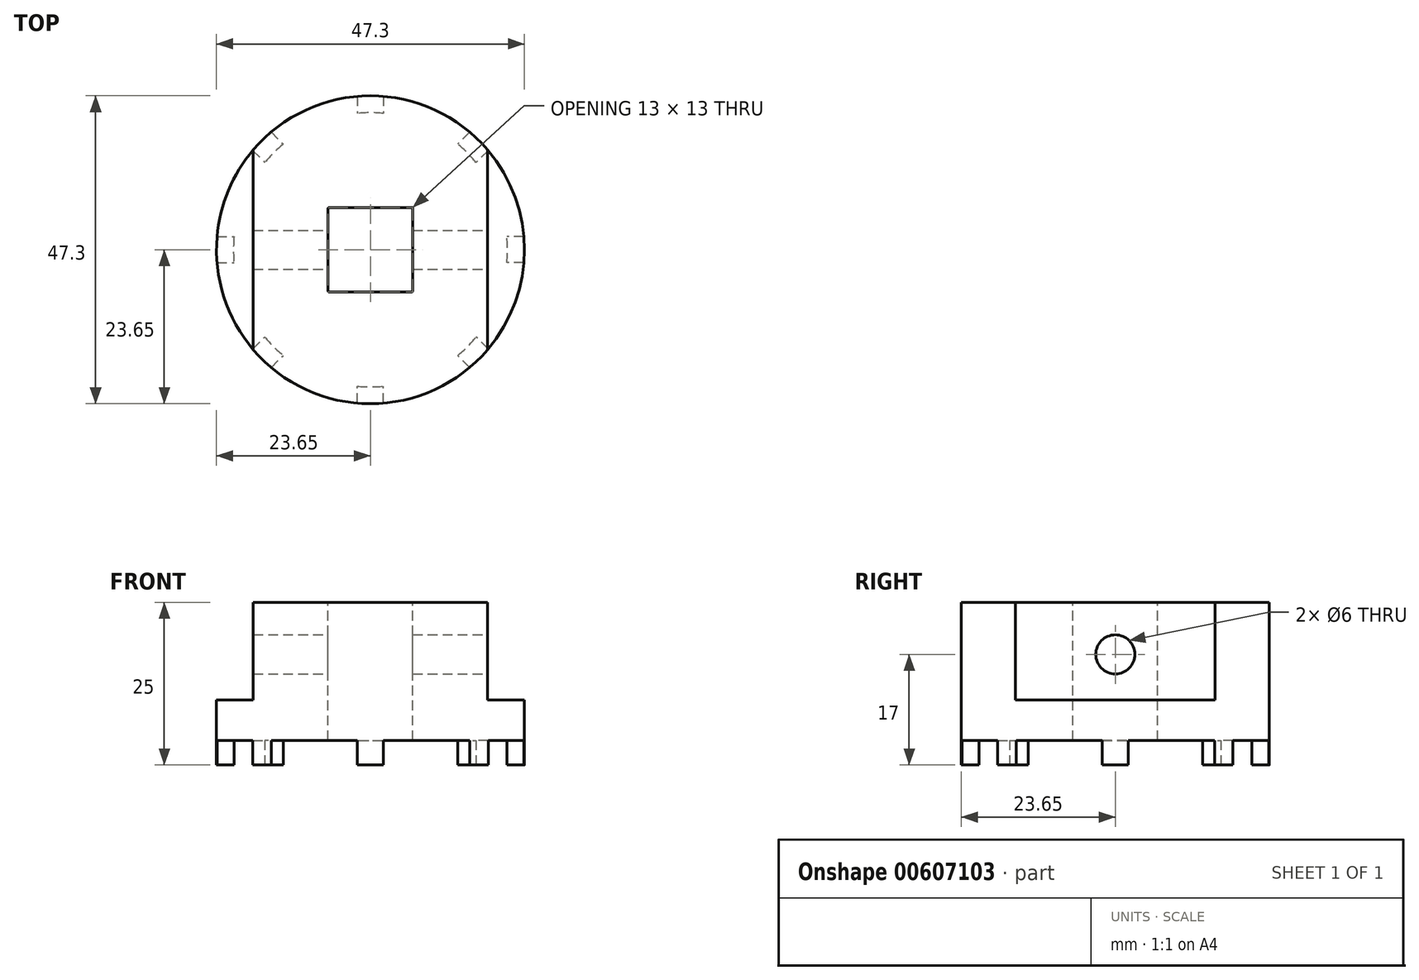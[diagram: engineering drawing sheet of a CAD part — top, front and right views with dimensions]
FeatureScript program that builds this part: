
annotation { "Feature Type Name" : "Feature", "Feature Type Description" : "" }
export const myFeature = defineFeature(function(context is Context, id is Id, definition is map)
    precondition{}
    {
        {
            var Q0;
            Q0=qCreatedBy(makeId("Top.planeOp"),FACE);
            var sketch = newSketch(context, id + "F0", { "sketchPlane" : qUnion([Q0])});
            skCircle(sketch, "E0", {"center": v(0, 0) * mm, "radius": 23.65 * mm});
            skSolve(sketch);
        }
        {
            var Q0;
            Q0 = qSketchRegion(id + "F0", true);
            extrude(context, id + "F1", {"entities" : qUnion([Q0]), "depth" : 25 * mm, "offsetDistance" : 25 * mm});
        }
        {
            var Q0;
            Q0=makeQuery(id+"F1.opExtrude","CAP_FACE",FACE,{"disambiguationData":[OSD([sQuery(id+"F0.wireOp",EDGE,"E0")])],"isStart":true});
            var sketch = newSketch(context, id + "F2", { "sketchPlane" : qUnion([Q0])});
            skCircle(sketch, "E1.0", {"center": v(0, 0) * mm, "radius": 23.65 * mm});
            skCircle(sketch, "E2", {"center": v(0, 0) * mm, "radius": 21.05 * mm});
            skLineSegment(sketch, "E3", {"start": v(-2, 23.57) * mm, "end": v(-2, 20.95) * mm});
            skLineSegment(sketch, "E4", {"start": v(2, 23.57) * mm, "end": v(2, 20.95) * mm});
            skLineSegment(sketch, "E5.1.0", {"start": v(-18.08, 15.25) * mm, "end": v(-16.23, 13.4) * mm});
            skLineSegment(sketch, "E5.1.1", {"start": v(-15.25, 18.08) * mm, "end": v(-13.4, 16.23) * mm});
            skLineSegment(sketch, "E5.2.0", {"start": v(-23.57, -2) * mm, "end": v(-20.95, -2) * mm});
            skLineSegment(sketch, "E5.2.1", {"start": v(-23.57, 2) * mm, "end": v(-20.95, 2) * mm});
            skLineSegment(sketch, "E5.3.0", {"start": v(-15.25, -18.08) * mm, "end": v(-13.4, -16.23) * mm});
            skLineSegment(sketch, "E5.3.1", {"start": v(-18.08, -15.25) * mm, "end": v(-16.23, -13.4) * mm});
            skLineSegment(sketch, "E5.4.0", {"start": v(2, -23.57) * mm, "end": v(2, -20.95) * mm});
            skLineSegment(sketch, "E5.4.1", {"start": v(-2, -23.57) * mm, "end": v(-2, -20.95) * mm});
            skLineSegment(sketch, "E5.5.0", {"start": v(18.08, -15.25) * mm, "end": v(16.23, -13.4) * mm});
            skLineSegment(sketch, "E5.5.1", {"start": v(15.25, -18.08) * mm, "end": v(13.4, -16.23) * mm});
            skLineSegment(sketch, "E5.6.0", {"start": v(23.57, 2) * mm, "end": v(20.95, 2) * mm});
            skLineSegment(sketch, "E5.6.1", {"start": v(23.57, -2) * mm, "end": v(20.95, -2) * mm});
            skLineSegment(sketch, "E5.7.0", {"start": v(15.25, 18.08) * mm, "end": v(13.4, 16.23) * mm});
            skLineSegment(sketch, "E5.7.1", {"start": v(18.08, 15.25) * mm, "end": v(16.23, 13.4) * mm});
            skSolve(sketch);
        }
        {
            var Q0;
            {var subQ0=sQuery(id+"F2.wireOp",EDGE,"E3");Q0=makeQuery(id+"F2.imprint","IMPRINT",FACE,{"disambiguationData":[TD([[makeQuery(id+"F2.imprint","IMPRINT",EDGE,{"derivedFrom":subQ0}),-1.0]])]});}
            var Q1;
            {var subQ0=sQuery(id+"F2.wireOp",EDGE,"E2");var subQ8=makeQuery(id+"F2.imprint","INTERSECT",VERTEX,{"derivedFrom":[subQ0,sQuery(id+"F2.wireOp",EDGE,"E5.6.0")]});Q1=makeQuery(id+"F2.imprint","IMPRINT",FACE,{"disambiguationData":[TD([[makeQuery(id+"F2.imprint","IMPRINT",EDGE,{"disambiguationData":[TD([[subQ8,-1.0]])],"derivedFrom":subQ0}),1.0]])]});}
            var Q2;
            {var subQ0=sQuery(id+"F2.wireOp",EDGE,"E5.1.0");Q2=makeQuery(id+"F2.imprint","IMPRINT",FACE,{"disambiguationData":[TD([[makeQuery(id+"F2.imprint","IMPRINT",EDGE,{"derivedFrom":subQ0}),-1.0]])]});}
            var Q3;
            {var subQ0=sQuery(id+"F2.wireOp",EDGE,"E5.2.0");Q3=makeQuery(id+"F2.imprint","IMPRINT",FACE,{"disambiguationData":[TD([[makeQuery(id+"F2.imprint","IMPRINT",EDGE,{"derivedFrom":subQ0}),-1.0]])]});}
            var Q4;
            {var subQ0=sQuery(id+"F2.wireOp",EDGE,"E5.3.0");Q4=makeQuery(id+"F2.imprint","IMPRINT",FACE,{"disambiguationData":[TD([[makeQuery(id+"F2.imprint","IMPRINT",EDGE,{"derivedFrom":subQ0}),-1.0]])]});}
            var Q5;
            {var subQ0=sQuery(id+"F2.wireOp",EDGE,"E5.4.0");Q5=makeQuery(id+"F2.imprint","IMPRINT",FACE,{"disambiguationData":[TD([[makeQuery(id+"F2.imprint","IMPRINT",EDGE,{"derivedFrom":subQ0}),-1.0]])]});}
            var Q6;
            {var subQ0=sQuery(id+"F2.wireOp",EDGE,"E5.5.0");Q6=makeQuery(id+"F2.imprint","IMPRINT",FACE,{"disambiguationData":[TD([[makeQuery(id+"F2.imprint","IMPRINT",EDGE,{"derivedFrom":subQ0}),-1.0]])]});}
            var Q7;
            {var subQ0=sQuery(id+"F2.wireOp",EDGE,"E5.6.0");Q7=makeQuery(id+"F2.imprint","IMPRINT",FACE,{"disambiguationData":[TD([[makeQuery(id+"F2.imprint","IMPRINT",EDGE,{"derivedFrom":subQ0}),-1.0]])]});}
            var Q8;
            {var subQ0=sQuery(id+"F2.wireOp",EDGE,"E4");Q8=makeQuery(id+"F2.imprint","IMPRINT",FACE,{"disambiguationData":[TD([[makeQuery(id+"F2.imprint","IMPRINT",EDGE,{"derivedFrom":subQ0}),1.0]])]});}
            extrude(context, id + "F3", {"entities" : qUnion([Q0, Q1, Q2, Q3, Q4, Q5, Q6, Q7, Q8]), "operationType" : NewBodyOperationType.REMOVE, "oppositeDirection" : true, "depth" : 3.8 * mm, "offsetDistance" : 25 * mm});
        }
        {
            var Q0;
            Q0=makeQuery(id+"F1.opExtrude","CAP_FACE",FACE,{"disambiguationData":[OSD([sQuery(id+"F0.wireOp",EDGE,"E0")])],"isStart":false});
            var sketch = newSketch(context, id + "F4", { "sketchPlane" : qUnion([Q0])});
            skArc(sketch, "E6.0", {"start": v(-18, 15.34) * mm, "mid": v(-23.65, 0) * mm, "end": v(-18, -15.34) * mm});
            skLineSegment(sketch, "E7", {"start": v(-18, 15.34) * mm, "end": v(-18, -15.34) * mm});
            skLineSegment(sketch, "E8", {"start": v(18, -15.34) * mm, "end": v(18, 15.34) * mm});
            skArc(sketch, "E9.trimOffspring", {"start": v(18, -15.34) * mm, "mid": v(23.65, 0) * mm, "end": v(18, 15.34) * mm});
            skSolve(sketch);
        }
        {
            var Q0;
            Q0 = qSketchRegion(id + "F4", true);
            extrude(context, id + "F5", {"entities" : qUnion([Q0]), "operationType" : NewBodyOperationType.REMOVE, "oppositeDirection" : true, "depth" : 15 * mm, "offsetDistance" : 25 * mm});
        }
        {
            var Q0;
            Q0=makeQuery(id+"F1.opExtrude","CAP_FACE",FACE,{"disambiguationData":[OSD([sQuery(id+"F0.wireOp",EDGE,"E0")])],"isStart":false});
            var sketch = newSketch(context, id + "F6", { "sketchPlane" : qUnion([Q0])});
            skLineSegment(sketch, "E10.bottom", {"start": v(6.5, -6.5) * mm, "end": v(-6.5, -6.5) * mm});
            skLineSegment(sketch, "E10.top", {"start": v(6.5, 6.5) * mm, "end": v(-6.5, 6.5) * mm});
            skLineSegment(sketch, "E10.left", {"start": v(6.5, -6.5) * mm, "end": v(6.5, 6.5) * mm});
            skLineSegment(sketch, "E10.right", {"start": v(-6.5, -6.5) * mm, "end": v(-6.5, 6.5) * mm});
            skPoint(sketch, "E10.middle", {"position": v(0, 0) * mm});
            skSolve(sketch);
        }
        {
            var Q0;
            Q0 = qSketchRegion(id + "F6", true);
            extrude(context, id + "F7", {"entities" : qUnion([Q0]), "operationType" : NewBodyOperationType.REMOVE, "endBound" : BoundingType.THROUGH_ALL, "oppositeDirection" : true, "depth" : 25 * mm, "offsetDistance" : 25 * mm});
        }
        {
            var Q0;
            Q0=makeQuery(id+"F7.boolean.opBoolean","COPY",EDGE,{"derivedFrom":makeQuery(id+"F7.opExtrude","SWEPT_EDGE",EDGE,{"disambiguationData":[OSD([sQuery(id+"F6.wireOp",EDGE,"E10.top"),sQuery(id+"F6.wireOp",EDGE,"E10.right")])]})});
            var Q1;
            Q1=makeQuery(id+"F7.boolean.opBoolean","COPY",EDGE,{"derivedFrom":makeQuery(id+"F7.opExtrude","SWEPT_EDGE",EDGE,{"disambiguationData":[OSD([sQuery(id+"F6.wireOp",EDGE,"E10.bottom"),sQuery(id+"F6.wireOp",EDGE,"E10.right")])]})});
            var Q2;
            Q2=makeQuery(id+"F7.boolean.opBoolean","COPY",EDGE,{"derivedFrom":makeQuery(id+"F7.opExtrude","SWEPT_EDGE",EDGE,{"disambiguationData":[OSD([sQuery(id+"F6.wireOp",EDGE,"E10.top"),sQuery(id+"F6.wireOp",EDGE,"E10.left")])]})});
            var Q3;
            Q3=makeQuery(id+"F7.boolean.opBoolean","COPY",EDGE,{"derivedFrom":makeQuery(id+"F7.opExtrude","SWEPT_EDGE",EDGE,{"disambiguationData":[OSD([sQuery(id+"F6.wireOp",EDGE,"E10.bottom"),sQuery(id+"F6.wireOp",EDGE,"E10.left")])]})});
            fillet(context, id + "F8", {"entities" : qUnion([Q0, Q1, Q2, Q3]), "radius" : 0.15 * mm, "tangentPropagation" : true, "allowEdgeOverflow" : false});
        }
        {
            var Q0;
            Q0=makeQuery(id+"F5.boolean.opBoolean","COPY",FACE,{"derivedFrom":makeQuery(id+"F5.opExtrude","SWEPT_FACE",FACE,{"disambiguationData":[OSD([sQuery(id+"F4.wireOp",EDGE,"E8")])]})});
            var sketch = newSketch(context, id + "F9", { "sketchPlane" : qUnion([Q0])});
            skCircle(sketch, "E11", {"center": v(0, 17) * mm, "radius": 3 * mm});
            skSolve(sketch);
        }
        {
            var Q0;
            Q0 = qSketchRegion(id + "F9", true);
            extrude(context, id + "F10", {"entities" : qUnion([Q0]), "operationType" : NewBodyOperationType.REMOVE, "endBound" : BoundingType.THROUGH_ALL, "oppositeDirection" : true, "depth" : 25 * mm, "offsetDistance" : 25 * mm});
        }
    });
